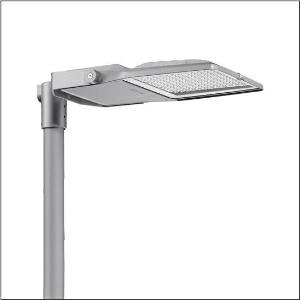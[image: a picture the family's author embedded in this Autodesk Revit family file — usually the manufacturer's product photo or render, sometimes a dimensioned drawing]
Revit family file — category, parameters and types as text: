
# Revit family: floodlight_fl_21_iq_midi___pl61_5xa7782f2c3a_b633
name_source: partatom
category: Lighting Fixtures
units: mm (PartAtom-declared; Revit-internal decimal feet)

## family parameters
Cut with Voids When Loaded = No
Host = Face
Light Source = No
Part Type = Normal
Room Calculation Point = No
Round Connector Dimension = Use Diameter
Shared = No

## types (1)
- --- (1 x LED, 35100 lm, 270.2 W, 3000K)
    Apparent Load = 270 VA
    CIE Flux Codes = 33 65 98 100 100
    Color Rendering = 70
    Color Temperature = 3000K
    Default Elevation = 1800 mm
    Description = Floodlight FL 21 iQ midi, floodlight, primary light control with lens, of PMMA, primary optical cover: protective disc, of toughened safety glass, transparent, light distribution: PL61, light emission: direct distribution, installation type: surface-mounted, LED, High Power LED, rated luminous flux: 35.100lm, luminous efficacy: 130lm/W, light colour: 730, colour temperature: 3000K, control gear: ECG iQ, control: optimised constant luminous flux control (CLO 2.0), Desk-Remote (wireless, voltage-free reading and setting of iQ features in the workshop via application-optimized NFC function/RFID function), Smart-Wire, Night-Set, Temp-Guard, Auto-Match, Street-Remote, with terminal, 6-pole, mains connection: 220..240V, AC, 50/60Hz, start of lifetime: 270W, end of service life: 287W, reduction: 117W, luminaire housing, of diecast aluminium, powder-coated, Siteco® metallic grey (DB 702S), corrosivity category C5 mid according to DIN EN ISO 12944, sealing non-destructively replaceable, please order mast flange separately, mast bracket, of steel, galvanised, powder-coated, Siteco® metallic grey (DB 702S), protection rating (complete): IP66, insulation class (complete): insulation class II (safety insulation), certification: CE, protection symbol: D, impact resistance: IK08, permissible operating ambient temperature: -40..+40°C, permissible operating ambient temperature for outdoor applications: -40..+50°C, standard: DIN EN 12944, LABS conformity tested according to VDMA 24364:2018-05, packaging unit: 1 piece

Light Distribution: PL61
    Height = 76 mm
    Lamp = 1 x LED
    Lamp Light Flux = 35100 lm
    Lamp Power = 270.2 W
    Lamp count = 1
    Length = 657 mm
    Luminous efficacy = 130 lm/W
    Manufacturer = Siteco
    ModVariant = No
    Model = 5XA7782F2C3A
    Number of Poles = 1
    OnlyDefault = Yes
    Power Factor = 1
    Product Name = Floodlight FL 21 iQ midi | PL61
    Product group = floodlight | pylon annexe
    ProductGroupID = 6200
    Protection Class = Protection class II
    Protection Degree = IP 66
    RLX_Detail_Level = 1
    RLX_Emergency_Light_Flux = 0 lm
    RLX_Emergency_Type = 0
    RLX_Emergency_Type_DB = No
    RlxData = <blob elided: 153965 chars, md5=d07a0324>
    Socket = socket
    Standby Power = 0 W
    System Light Flux = 35100 lm
    System Power = 270 W
    Type Comments = factory setting: luminous flux: 100 % | dim-lin: 254 | 620 mA
    Type Image = l_1007123.jpg
    URL = http://relux.com
    VarID = @adj_038425
    Voltage = 0 V
    Weight = 0.00 kg
    Width = 442 mm

## geometry (parser evidence)
native form markers: Blend x4, Sweep x14
no freeform markers — native parametric forms only
